# Revit family: continental_V2
name_source: partatom
category: Furniture
revit_build: Autodesk Revit 2015 (Build: 20140903_1530(x64)
units: mm (PartAtom-declared; Revit-internal decimal feet)

## types (10) — shared parameters
BIMobject category = Armchairs
BOSUseNativeGeometries = 1
Brand url = http://www.swedese.com
Date of publishing = 3/22/2016
Design country = Sweden
Edition number = 1
IFC Classification = Furnishing Element
Manufacturer country = Sweden
Manufacturer name = Swedese
Material main = Fabric
Material secondary = Steel
Nominal height = 720
Nominal width = 910
OmniClass Code = 23-21 11 00
OmniClass Description = Commercial Furniture
Product Guid = e6af1e70-cf06-4887-830f-37ebb6f2d1fe
Product SKU = 15301
Product data url = https://bimobject.com
Product family = Easy chairs
Product group = Continental
Product name = Continental
Product url = http://www.swedese.se
QR code = http://bimobject.com
Technical description = https://static-swedese.s3.amazonaws.com
UNSPSC Code = 56
Uniclass 1.4 Code = L8211
Uniclass 1.4 Description = Furniture
Weight Net (Kg) = 34

## type names (no varying parameters)
- Legs - (Black) COLOUR - (Brown)
- Legs - (Chrome) COLOUR - (Brown)
- Legs - (Black) COLOUR - (Dark Green)
- Legs - (Chrome) COLOUR - (Dark Green)
- Legs - (Black) COLOUR - (Green)
- Legs - (Chrome) COLOUR - (Green)
- Legs - (Black) COLOUR - (Blue)
- Legs - (Chrome) COLOUR - (Blue)
- Legs - (Black) COLOUR - (Light Brown)
- Legs - (Chrome) COLOUR - (Light Brown)

## geometry (parser evidence)
native form markers: Sweep x1
no freeform markers — native parametric forms only
